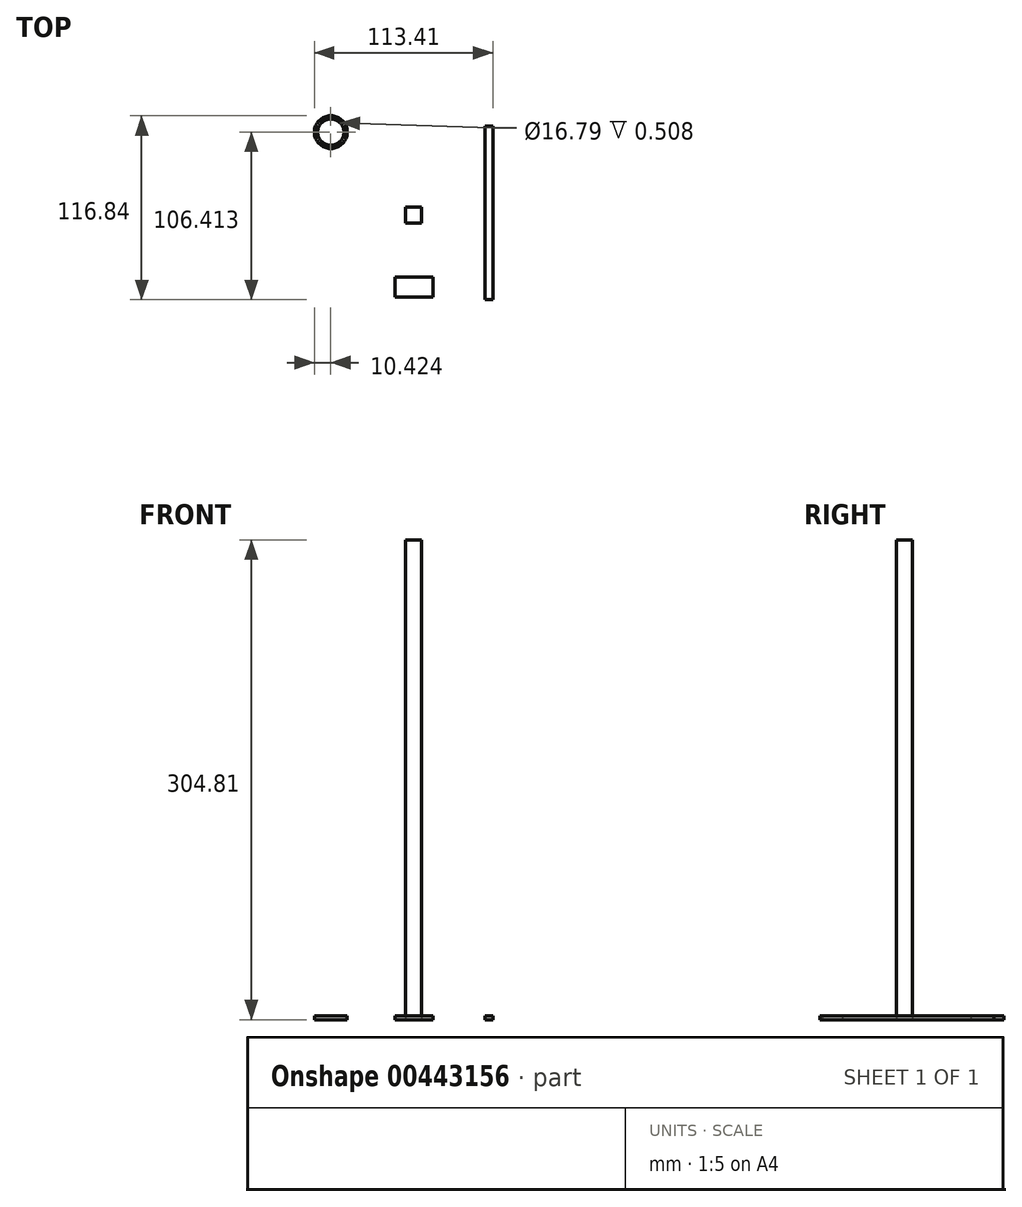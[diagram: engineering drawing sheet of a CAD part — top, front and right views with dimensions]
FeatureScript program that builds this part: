
annotation { "Feature Type Name" : "Feature", "Feature Type Description" : "" }
export const myFeature = defineFeature(function(context is Context, id is Id, definition is map)
    precondition{}
    {
        {
            var Q0;
            Q0=qCreatedBy(makeId("Front.planeOp"),FACE);
            var sketch = newSketch(context, id + "F0", { "sketchPlane" : qUnion([Q0])});
            skLineSegment(sketch, "E0", {"start": v(-48, 0.01) * mm, "end": v(104.4, 0.01) * mm});
            skSolve(sketch);
        }
        {
            var Q0;
            Q0=sQuery(id+"F0.wireOp",EDGE,"E0");
            extrude(context, id + "F1", {"bodyType" : ToolBodyType.SURFACE, "surfaceEntities" : qUnion([Q0]), "oppositeDirection" : true, "depth" : 152.4 * mm});
        }
        {
            var Q0;
            Q0=makeQuery(id+"F1.opExtrude","SWEPT_FACE",FACE,{"disambiguationData":[OSD([sQuery(id+"F0.wireOp",EDGE,"E0")])]});
            var sketch = newSketch(context, id + "F2", { "sketchPlane" : qUnion([Q0])});
            skLineSegment(sketch, "E1", {"start": v(22.35, 81.26) * mm, "end": v(22.35, 71.1) * mm});
            skLineSegment(sketch, "E2", {"start": v(22.35, 71.1) * mm, "end": v(32.5, 71.1) * mm});
            skLineSegment(sketch, "E3", {"start": v(32.5, 71.1) * mm, "end": v(32.5, 81.26) * mm});
            skLineSegment(sketch, "E4", {"start": v(32.5, 81.26) * mm, "end": v(22.35, 81.26) * mm});
            skSolve(sketch);
        }
        {
            var Q0;
            Q0 = qSketchRegion(id + "F2", true);
            extrude(context, id + "F3", {"entities" : qUnion([Q0]), "depth" : 304.8 * mm});
        }
        {
            var Q0;
            Q0=qCreatedBy(makeId("Top.planeOp"),FACE);
            var sketch = newSketch(context, id + "F4", { "sketchPlane" : qUnion([Q0])});
            skLineSegment(sketch, "E5.bottom", {"start": v(15.75, 36.68) * mm, "end": v(39.94, 36.68) * mm});
            skLineSegment(sketch, "E5.top", {"start": v(15.75, 24.13) * mm, "end": v(39.94, 24.13) * mm});
            skLineSegment(sketch, "E5.left", {"start": v(15.75, 36.68) * mm, "end": v(15.75, 24.13) * mm});
            skLineSegment(sketch, "E5.right", {"start": v(39.94, 36.68) * mm, "end": v(39.94, 24.13) * mm});
            skSolve(sketch);
        }
        {
            var Q0;
            Q0 = qSketchRegion(id + "F4", true);
            extrude(context, id + "F5", {"entities" : qUnion([Q0]), "depth" : 2.54 * mm});
        }
        {
            var Q0;
            Q0=qCreatedBy(makeId("Top.planeOp"),FACE);
            var sketch = newSketch(context, id + "F6", { "sketchPlane" : qUnion([Q0])});
            skLineSegment(sketch, "E6.bottom", {"start": v(72.85, 132.78) * mm, "end": v(78.01, 132.78) * mm});
            skLineSegment(sketch, "E6.top", {"start": v(72.85, 22.42) * mm, "end": v(78.01, 22.42) * mm});
            skLineSegment(sketch, "E6.left", {"start": v(72.85, 132.78) * mm, "end": v(72.85, 22.42) * mm});
            skLineSegment(sketch, "E6.right", {"start": v(78.01, 132.78) * mm, "end": v(78.01, 22.42) * mm});
            skSolve(sketch);
        }
        {
            var Q0;
            Q0 = qSketchRegion(id + "F6", true);
            extrude(context, id + "F7", {"entities" : qUnion([Q0]), "depth" : 2.54 * mm});
        }
        {
            var Q0;
            Q0=qCreatedBy(makeId("Top.planeOp"),FACE);
            var sketch = newSketch(context, id + "F8", { "sketchPlane" : qUnion([Q0])});
            skCircle(sketch, "E7", {"center": v(-24.98, 128.83) * mm, "radius": 10.43 * mm});
            skSolve(sketch);
        }
        {
            var Q0;
            Q0 = qSketchRegion(id + "F8", true);
            extrude(context, id + "F9", {"entities" : qUnion([Q0]), "depth" : 2.54 * mm});
        }
        {
            var Q0;
            Q0=makeQuery(id+"F9.opExtrude","CAP_FACE",FACE,{"disambiguationData":[OSD([sQuery(id+"F8.wireOp",EDGE,"E7")])],"isStart":false});
            shell(context, id + "F10", {"entities" : qUnion([Q0]), "thickness" : 2.54 * mm});
        }
        {
            var Q0;
            Q0=makeQuery(id+"F9.opExtrude","CAP_FACE",FACE,{"disambiguationData":[OSD([sQuery(id+"F8.wireOp",EDGE,"E7")])],"isStart":false});
            shell(context, id + "F11", {"entities" : qUnion([Q0]), "thickness" : 2.03 * mm});
        }
    });
